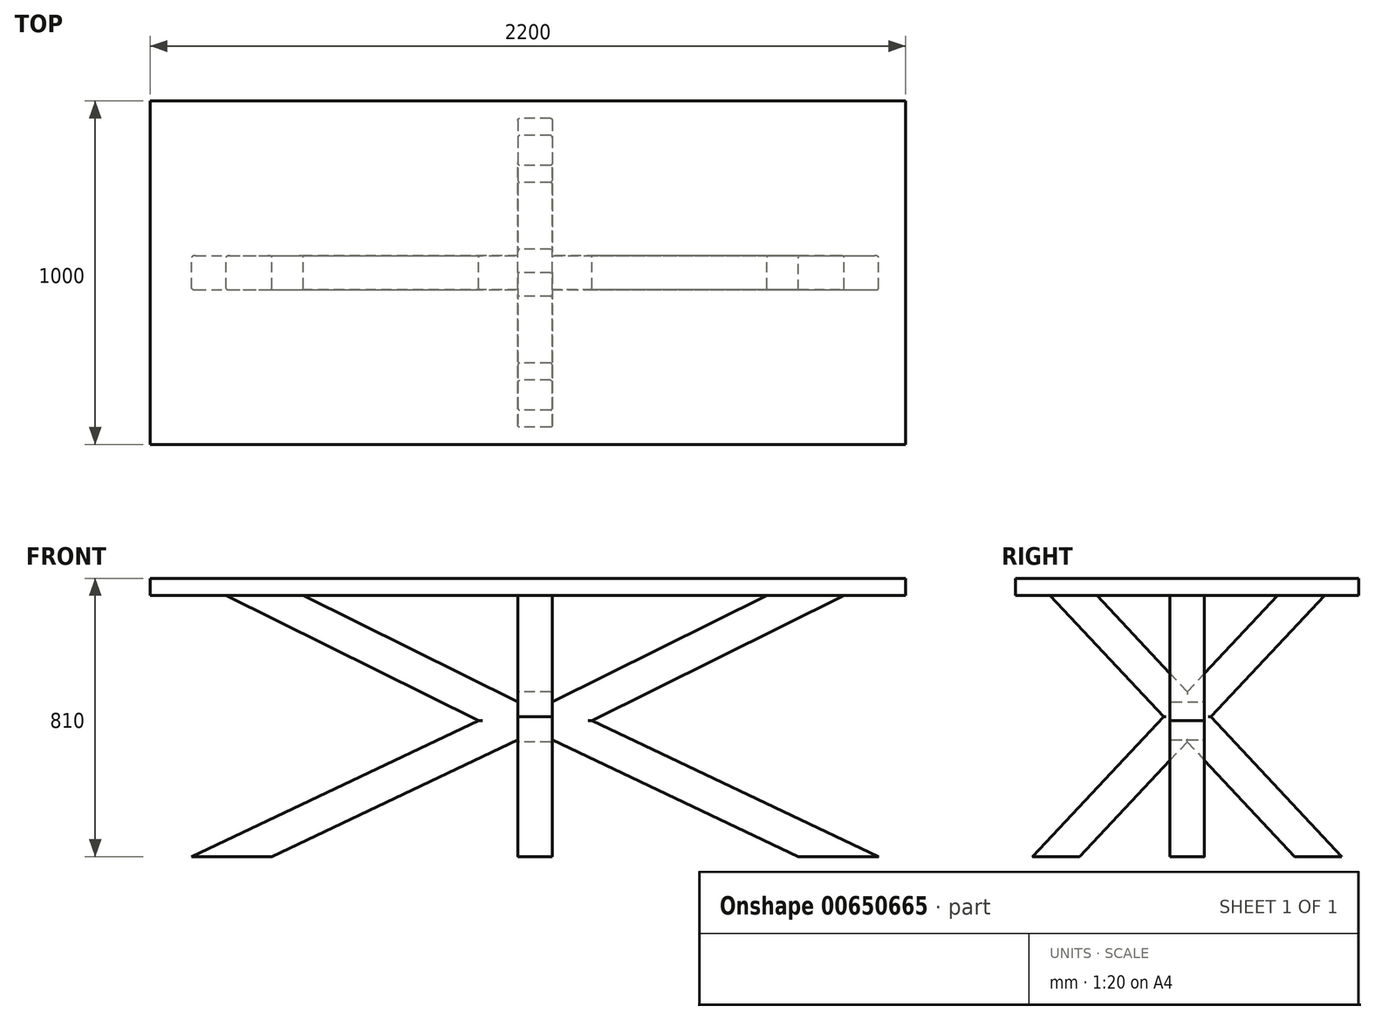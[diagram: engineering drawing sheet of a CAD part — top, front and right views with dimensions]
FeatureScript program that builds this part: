
annotation { "Feature Type Name" : "Feature", "Feature Type Description" : "" }
export const myFeature = defineFeature(function(context is Context, id is Id, definition is map)
    precondition{}
    {
        {
            var Q0;
            Q0=qCreatedBy(makeId("Front.planeOp"),FACE);
            var sketch = newSketch(context, id + "F0", { "sketchPlane" : qUnion([Q0])});
            skLineSegment(sketch, "E0.bottom", {"start": v(-1121.12, 360) * mm, "end": v(1078.88, 360) * mm});
            skLineSegment(sketch, "E0.top", {"start": v(-1121.12, 310) * mm, "end": v(1078.88, 310) * mm});
            skLineSegment(sketch, "E0.left", {"start": v(-1121.12, 360) * mm, "end": v(-1121.12, 310) * mm});
            skLineSegment(sketch, "E0.right", {"start": v(1078.88, 360) * mm, "end": v(1078.88, 310) * mm});
            skSolve(sketch);
        }
        {
            var Q0;
            Q0=makeQuery(id+"F0.imprint","IMPRINT",FACE,{"disambiguationData":[TD([[makeQuery(id+"F0.imprint","IMPRINT",EDGE,{"derivedFrom":sQuery(id+"F0.wireOp",EDGE,"E0.bottom")}),-1.0]])]});
            extrude(context, id + "F1", {"entities" : qUnion([Q0]), "endBound" : BoundingType.SYMMETRIC, "depth" : 1000 * mm, "offsetDistance" : 25 * mm});
        }
        {
            var Q0;
            Q0=qCreatedBy(makeId("Front.planeOp"),FACE);
            var sketch = newSketch(context, id + "F2", { "sketchPlane" : qUnion([Q0])});
            skLineSegment(sketch, "E1", {"start": v(-900, 310) * mm, "end": v(-674.96, 310) * mm});
            skLineSegment(sketch, "E2", {"start": v(-1000, -450) * mm, "end": v(-766.4, -450) * mm});
            skLineSegment(sketch, "E3", {"start": v(-50, 310) * mm, "end": v(-50, -450) * mm});
            skLineSegment(sketch, "E4", {"start": v(50, 310) * mm, "end": v(50, -450) * mm});
            skLineSegment(sketch, "E5", {"start": v(-1000, -450) * mm, "end": v(-50, 0) * mm});
            skLineSegment(sketch, "E6", {"start": v(50, 0) * mm, "end": v(1000, -450) * mm});
            skLineSegment(sketch, "E7", {"start": v(766.4, -450) * mm, "end": v(310.05, -233.84) * mm});
            skLineSegment(sketch, "E8", {"start": v(-766.4, -450) * mm, "end": v(-216.72, -189.62) * mm});
            skLineSegment(sketch, "E9", {"start": v(-216.72, -189.62) * mm, "end": v(-50, -110.65) * mm});
            skPoint(sketch, "E9.endSnap0", {"position": v(-50, -45.55) * mm});
            skLineSegment(sketch, "E10", {"start": v(310.05, -233.84) * mm, "end": v(50, -110.65) * mm});
            skLineSegment(sketch, "E11", {"start": v(-50, 0) * mm, "end": v(-674.96, 310) * mm});
            skLineSegment(sketch, "E12", {"start": v(-900, 310) * mm, "end": v(-165.11, -54.53) * mm});
            skLineSegment(sketch, "E13", {"start": v(50, 0) * mm, "end": v(674.96, 310) * mm});
            skLineSegment(sketch, "E14", {"start": v(900, 310) * mm, "end": v(165.11, -54.53) * mm});
            skLineSegment(sketch, "E15.trimOffspring", {"start": v(-50, -450) * mm, "end": v(50, -450) * mm});
            skPoint(sketch, "E16.orphan", {"position": v(-50, -545.51) * mm});
            skPoint(sketch, "E17.orphan", {"position": v(-50, 454.42) * mm});
            skLineSegment(sketch, "E18.trimOffspring", {"start": v(674.96, 310) * mm, "end": v(900, 310) * mm});
            skLineSegment(sketch, "E19.trimOffspring", {"start": v(-50, 310) * mm, "end": v(50, 310) * mm});
            skLineSegment(sketch, "E20.trimOffspring", {"start": v(766.4, -450) * mm, "end": v(1000, -450) * mm});
            skLineSegment(sketch, "E21", {"start": v(1000, -450) * mm, "end": v(802.41, -867.13) * mm});
            skSolve(sketch);
        }
        {
            var Q0;
            Q0=qCreatedBy(makeId("Right.planeOp"),FACE);
            var sketch = newSketch(context, id + "F3", { "sketchPlane" : qUnion([Q0])});
            skLineSegment(sketch, "E22", {"start": v(400, 310) * mm, "end": v(262.9, 310) * mm});
            skLineSegment(sketch, "E23", {"start": v(450, -450) * mm, "end": v(312.9, -450) * mm});
            skLineSegment(sketch, "E24", {"start": v(400, 310) * mm, "end": v(-312.9, -450) * mm});
            skLineSegment(sketch, "E25", {"start": v(-450, -450) * mm, "end": v(262.9, 310) * mm});
            skLineSegment(sketch, "E26", {"start": v(450, -450) * mm, "end": v(68.55, -43.35) * mm});
            skLineSegment(sketch, "E27", {"start": v(-400, 310) * mm, "end": v(-68.55, -43.35) * mm});
            skLineSegment(sketch, "E28.trimOffspring", {"start": v(0, -116.43) * mm, "end": v(312.9, -450) * mm});
            skLineSegment(sketch, "E29.trimOffspring", {"start": v(0, 29.74) * mm, "end": v(-262.9, 310) * mm});
            skLineSegment(sketch, "E30.trimOffspring", {"start": v(-262.9, 310) * mm, "end": v(-400, 310) * mm});
            skLineSegment(sketch, "E31.trimOffspring", {"start": v(-312.9, -450) * mm, "end": v(-450, -450) * mm});
            skSolve(sketch);
        }
        {
            var Q0;
            {var subQ0=sQuery(id+"F3.wireOp",EDGE,"E24");var subQ3=sQuery(id+"F3.wireOp",EDGE,"E22");var subQ4=makeQuery(id+"F3.imprint","INTERSECT",VERTEX,{"derivedFrom":[subQ3,subQ0]});Q0=makeQuery(id+"F3.imprint","IMPRINT",FACE,{"disambiguationData":[TD([[makeQuery(id+"F3.imprint","IMPRINT",EDGE,{"disambiguationData":[TD([[subQ4,-1.0]])],"derivedFrom":subQ3}),1.0]])]});}
            var Q1;
            {var subQ0=sQuery(id+"F3.wireOp",EDGE,"E26");Q1=makeQuery(id+"F3.imprint","IMPRINT",FACE,{"disambiguationData":[TD([[makeQuery(id+"F3.imprint","IMPRINT",EDGE,{"derivedFrom":subQ0}),1.0]])]});}
            var Q2;
            {var subQ0=sQuery(id+"F3.wireOp",EDGE,"E27");Q2=makeQuery(id+"F3.imprint","IMPRINT",FACE,{"disambiguationData":[TD([[makeQuery(id+"F3.imprint","IMPRINT",EDGE,{"derivedFrom":subQ0}),1.0]])]});}
            extrude(context, id + "F4", {"entities" : qUnion([Q0, Q1, Q2]), "endBound" : BoundingType.SYMMETRIC, "depth" : 100 * mm, "offsetDistance" : 25 * mm});
        }
        {
            var Q0;
            {var subQ4=sQuery(id+"F2.wireOp",EDGE,"E2");Q0=makeQuery(id+"F2.imprint","IMPRINT",FACE,{"disambiguationData":[TD([[makeQuery(id+"F2.imprint","IMPRINT",EDGE,{"derivedFrom":subQ4}),1.0]])]});}
            var Q1;
            {var subQ2=sQuery(id+"F2.wireOp",EDGE,"E11");Q1=makeQuery(id+"F2.imprint","IMPRINT",FACE,{"disambiguationData":[TD([[makeQuery(id+"F2.imprint","IMPRINT",EDGE,{"derivedFrom":subQ2}),1.0]])]});}
            var Q2;
            {var subQ0=sQuery(id+"F2.wireOp",EDGE,"E7");Q2=makeQuery(id+"F2.imprint","IMPRINT",FACE,{"disambiguationData":[TD([[makeQuery(id+"F2.imprint","IMPRINT",EDGE,{"derivedFrom":subQ0}),-1.0]])]});}
            var Q3;
            {var subQ2=sQuery(id+"F2.wireOp",EDGE,"E13");Q3=makeQuery(id+"F2.imprint","IMPRINT",FACE,{"disambiguationData":[TD([[makeQuery(id+"F2.imprint","IMPRINT",EDGE,{"derivedFrom":subQ2}),-1.0]])]});}
            extrude(context, id + "F5", {"entities" : qUnion([Q0, Q1, Q2, Q3]), "operationType" : NewBodyOperationType.ADD, "endBound" : BoundingType.SYMMETRIC, "depth" : 100 * mm, "offsetDistance" : 25 * mm});
        }
        {
            var Q0;
            Q0=makeQuery(id+"F5.opExtrude","CAP_EDGE",EDGE,{"disambiguationData":[OSD([sQuery(id+"F2.wireOp",EDGE,"E11")])],"isStart":false});
            var Q1;
            Q1=makeQuery(id+"F5.opExtrude","CAP_EDGE",EDGE,{"disambiguationData":[OSD([sQuery(id+"F2.wireOp",EDGE,"E12")])],"isStart":true});
            var Q2;
            Q2=makeQuery(id+"F5.opExtrude","CAP_EDGE",EDGE,{"disambiguationData":[OSD([sQuery(id+"F2.wireOp",EDGE,"E5")])],"isStart":false});
            var Q3;
            Q3=makeQuery(id+"F5.opExtrude","CAP_EDGE",EDGE,{"disambiguationData":[OSD([sQuery(id+"F2.wireOp",EDGE,"E8"),sQuery(id+"F2.wireOp",EDGE,"E9")])],"isStart":false});
            var Q4;
            Q4=makeQuery(id+"F5.opExtrude","CAP_EDGE",EDGE,{"disambiguationData":[OSD([sQuery(id+"F2.wireOp",EDGE,"E8"),sQuery(id+"F2.wireOp",EDGE,"E9")])],"isStart":true});
            var Q5;
            Q5=makeQuery(id+"F5.opExtrude","CAP_EDGE",EDGE,{"disambiguationData":[OSD([sQuery(id+"F2.wireOp",EDGE,"E5")])],"isStart":true});
            var Q6;
            {var subQ0=sQuery(id+"F3.wireOp",EDGE,"E24");Q6=makeQuery(id+"F4.opExtrude","CAP_EDGE",EDGE,{"disambiguationData":[OSD([subQ0]),TDD([makeQuery(id+"F3.imprint","IMPRINT",EDGE,{"disambiguationData":[TD([[makeQuery(id+"F3.imprint","INTERSECT",VERTEX,{"derivedFrom":[sQuery(id+"F3.wireOp",EDGE,"E22"),subQ0]}),-1.0]])],"derivedFrom":subQ0})])],"isStart":true});}
            var Q7;
            {var subQ0=sQuery(id+"F3.wireOp",EDGE,"E25");Q7=makeQuery(id+"F4.opExtrude","CAP_EDGE",EDGE,{"disambiguationData":[OSD([subQ0]),TDD([makeQuery(id+"F3.imprint","IMPRINT",EDGE,{"disambiguationData":[TD([[makeQuery(id+"F3.imprint","INTERSECT",VERTEX,{"derivedFrom":[sQuery(id+"F3.wireOp",EDGE,"E22"),subQ0]}),1.0]])],"derivedFrom":subQ0})])],"isStart":true});}
            var Q8;
            Q8=makeQuery(id+"F4.opExtrude","CAP_EDGE",EDGE,{"disambiguationData":[OSD([sQuery(id+"F3.wireOp",EDGE,"E26")])],"isStart":true});
            var Q9;
            Q9=makeQuery(id+"F4.opExtrude","CAP_EDGE",EDGE,{"disambiguationData":[OSD([sQuery(id+"F3.wireOp",EDGE,"E28.trimOffspring")])],"isStart":true});
            var Q10;
            {var subQ0=sQuery(id+"F3.wireOp",EDGE,"E24");Q10=makeQuery(id+"F4.opExtrude","CAP_EDGE",EDGE,{"disambiguationData":[OSD([subQ0]),TDD([makeQuery(id+"F3.imprint","IMPRINT",EDGE,{"disambiguationData":[TD([[makeQuery(id+"F3.imprint","INTERSECT",VERTEX,{"derivedFrom":[sQuery(id+"F3.wireOp",EDGE,"E23"),subQ0]}),1.0]])],"derivedFrom":subQ0})])],"isStart":true});}
            var Q11;
            {var subQ0=sQuery(id+"F3.wireOp",EDGE,"E25");Q11=makeQuery(id+"F4.opExtrude","CAP_EDGE",EDGE,{"disambiguationData":[OSD([subQ0]),TDD([makeQuery(id+"F3.imprint","IMPRINT",EDGE,{"disambiguationData":[TD([[makeQuery(id+"F3.imprint","INTERSECT",VERTEX,{"derivedFrom":[sQuery(id+"F3.wireOp",EDGE,"E23"),subQ0]}),-1.0]])],"derivedFrom":subQ0})])],"isStart":true});}
            var Q12;
            Q12=makeQuery(id+"F4.opExtrude","CAP_EDGE",EDGE,{"disambiguationData":[OSD([sQuery(id+"F3.wireOp",EDGE,"E26")])],"isStart":false});
            var Q13;
            Q13=makeQuery(id+"F4.opExtrude","CAP_EDGE",EDGE,{"disambiguationData":[OSD([sQuery(id+"F3.wireOp",EDGE,"E28.trimOffspring")])],"isStart":false});
            var Q14;
            Q14=makeQuery(id+"F5.opExtrude","CAP_EDGE",EDGE,{"disambiguationData":[OSD([sQuery(id+"F2.wireOp",EDGE,"E7"),sQuery(id+"F2.wireOp",EDGE,"E10")])],"isStart":true});
            var Q15;
            Q15=makeQuery(id+"F5.opExtrude","CAP_EDGE",EDGE,{"disambiguationData":[OSD([sQuery(id+"F2.wireOp",EDGE,"E6")])],"isStart":true});
            var Q16;
            Q16=makeQuery(id+"F5.opExtrude","CAP_EDGE",EDGE,{"disambiguationData":[OSD([sQuery(id+"F2.wireOp",EDGE,"E14")])],"isStart":true});
            var Q17;
            Q17=makeQuery(id+"F4.opExtrude","CAP_EDGE",EDGE,{"disambiguationData":[OSD([sQuery(id+"F3.wireOp",EDGE,"E29.trimOffspring")])],"isStart":false});
            var Q18;
            Q18=makeQuery(id+"F4.opExtrude","CAP_EDGE",EDGE,{"disambiguationData":[OSD([sQuery(id+"F3.wireOp",EDGE,"E29.trimOffspring")])],"isStart":true});
            var Q19;
            {var subQ0=sQuery(id+"F3.wireOp",EDGE,"E25");Q19=makeQuery(id+"F4.opExtrude","CAP_EDGE",EDGE,{"disambiguationData":[OSD([subQ0]),TDD([makeQuery(id+"F3.imprint","IMPRINT",EDGE,{"disambiguationData":[TD([[makeQuery(id+"F3.imprint","INTERSECT",VERTEX,{"derivedFrom":[sQuery(id+"F3.wireOp",EDGE,"E23"),subQ0]}),-1.0]])],"derivedFrom":subQ0})])],"isStart":false});}
            var Q20;
            {var subQ0=sQuery(id+"F3.wireOp",EDGE,"E24");Q20=makeQuery(id+"F4.opExtrude","CAP_EDGE",EDGE,{"disambiguationData":[OSD([subQ0]),TDD([makeQuery(id+"F3.imprint","IMPRINT",EDGE,{"disambiguationData":[TD([[makeQuery(id+"F3.imprint","INTERSECT",VERTEX,{"derivedFrom":[sQuery(id+"F3.wireOp",EDGE,"E23"),subQ0]}),1.0]])],"derivedFrom":subQ0})])],"isStart":false});}
            var Q21;
            Q21=makeQuery(id+"F4.opExtrude","CAP_EDGE",EDGE,{"disambiguationData":[OSD([sQuery(id+"F3.wireOp",EDGE,"E27")])],"isStart":false});
            var Q22;
            Q22=makeQuery(id+"F4.opExtrude","CAP_EDGE",EDGE,{"disambiguationData":[OSD([sQuery(id+"F3.wireOp",EDGE,"E27")])],"isStart":true});
            var Q23;
            Q23=makeQuery(id+"F5.opExtrude","CAP_EDGE",EDGE,{"disambiguationData":[OSD([sQuery(id+"F2.wireOp",EDGE,"E12")])],"isStart":false});
            var Q24;
            {var subQ0=sQuery(id+"F3.wireOp",EDGE,"E24");Q24=makeQuery(id+"F4.opExtrude","CAP_EDGE",EDGE,{"disambiguationData":[OSD([subQ0]),TDD([makeQuery(id+"F3.imprint","IMPRINT",EDGE,{"disambiguationData":[TD([[makeQuery(id+"F3.imprint","INTERSECT",VERTEX,{"derivedFrom":[sQuery(id+"F3.wireOp",EDGE,"E22"),subQ0]}),-1.0]])],"derivedFrom":subQ0})])],"isStart":false});}
            var Q25;
            {var subQ0=sQuery(id+"F3.wireOp",EDGE,"E25");Q25=makeQuery(id+"F4.opExtrude","CAP_EDGE",EDGE,{"disambiguationData":[OSD([subQ0]),TDD([makeQuery(id+"F3.imprint","IMPRINT",EDGE,{"disambiguationData":[TD([[makeQuery(id+"F3.imprint","INTERSECT",VERTEX,{"derivedFrom":[sQuery(id+"F3.wireOp",EDGE,"E22"),subQ0]}),1.0]])],"derivedFrom":subQ0})])],"isStart":false});}
            var Q26;
            Q26=makeQuery(id+"F5.opExtrude","CAP_EDGE",EDGE,{"disambiguationData":[OSD([sQuery(id+"F2.wireOp",EDGE,"E13")])],"isStart":true});
            var Q27;
            Q27=makeQuery(id+"F5.opExtrude","CAP_EDGE",EDGE,{"disambiguationData":[OSD([sQuery(id+"F2.wireOp",EDGE,"E13")])],"isStart":false});
            var Q28;
            Q28=makeQuery(id+"F5.opExtrude","CAP_EDGE",EDGE,{"disambiguationData":[OSD([sQuery(id+"F2.wireOp",EDGE,"E11")])],"isStart":true});
            var Q29;
            Q29=makeQuery(id+"F5.opExtrude","CAP_EDGE",EDGE,{"disambiguationData":[OSD([sQuery(id+"F2.wireOp",EDGE,"E6")])],"isStart":false});
            var Q30;
            Q30=makeQuery(id+"F5.opExtrude","CAP_EDGE",EDGE,{"disambiguationData":[OSD([sQuery(id+"F2.wireOp",EDGE,"E14")])],"isStart":false});
            fillet(context, id + "F6", {"entities" : qUnion([Q0, Q1, Q2, Q3, Q4, Q5, Q6, Q7, Q8, Q9, Q10, Q11, Q12, Q13, Q14, Q15, Q16, Q17, Q18, Q19, Q20, Q21, Q22, Q23, Q24, Q25, Q26, Q27, Q28, Q29, Q30]), "radius" : 5 * mm, "tangentPropagation" : true, "allowEdgeOverflow" : false});
        }
    });
